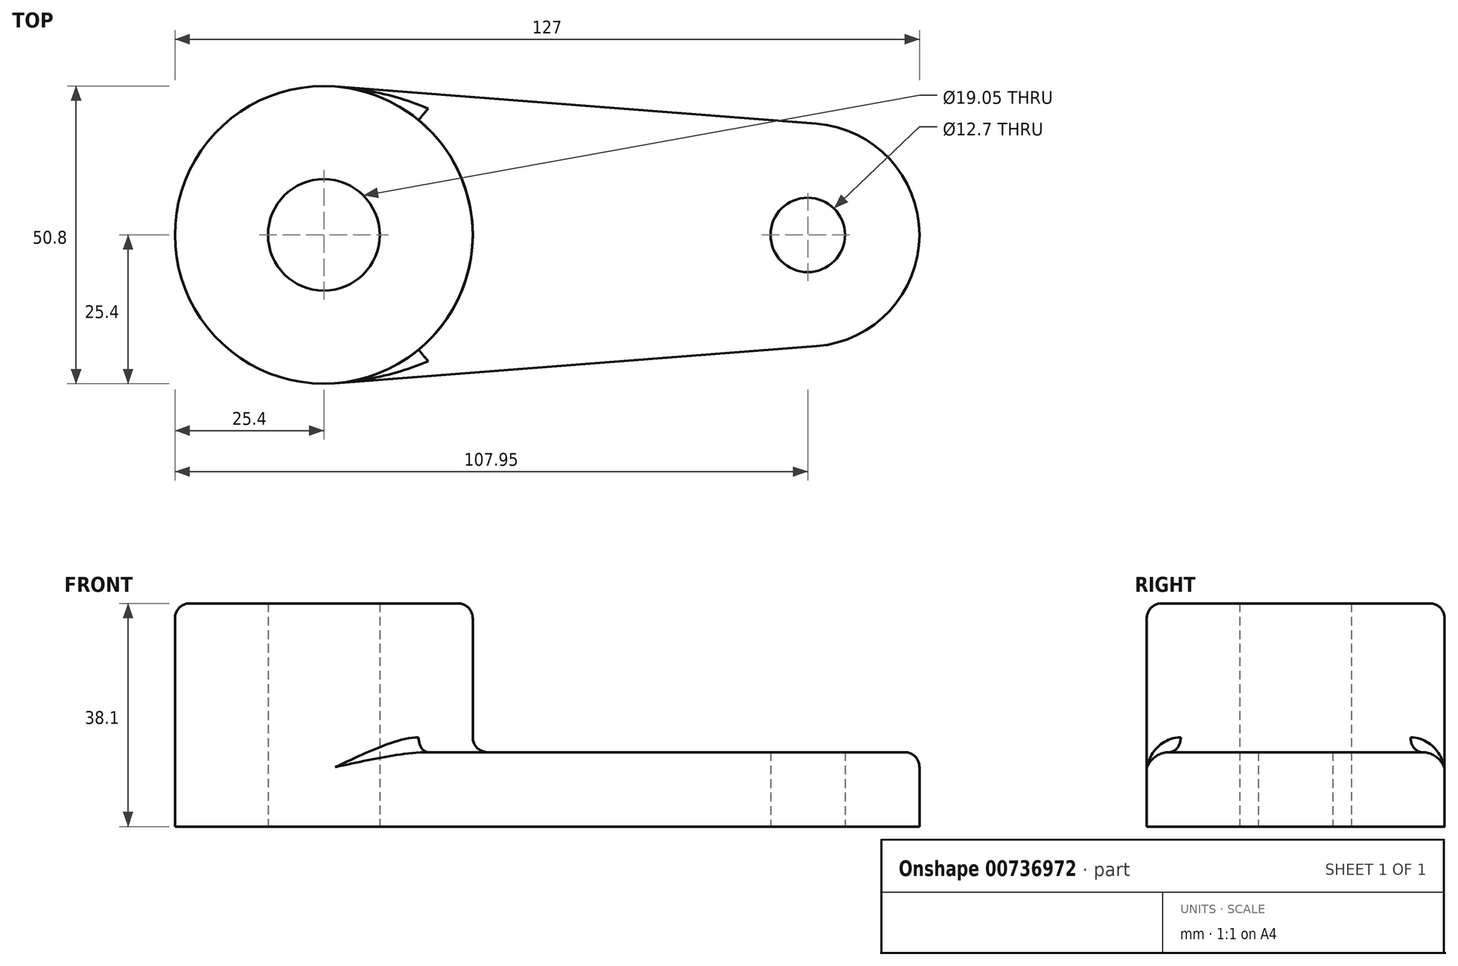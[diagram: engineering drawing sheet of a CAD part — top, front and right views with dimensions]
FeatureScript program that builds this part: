
annotation { "Feature Type Name" : "Feature", "Feature Type Description" : "" }
export const myFeature = defineFeature(function(context is Context, id is Id, definition is map)
    precondition{}
    {
        {
            var Q0;
            Q0=qCreatedBy(makeId("Top.planeOp"),FACE);
            var sketch = newSketch(context, id + "F0", { "sketchPlane" : qUnion([Q0])});
            skCircle(sketch, "E0", {"center": v(0, 0) * mm, "radius": 25.4 * mm});
            skCircle(sketch, "E1", {"center": v(82.55, 0) * mm, "radius": 19.05 * mm});
            skCircle(sketch, "E2", {"center": v(0, 0) * mm, "radius": 9.53 * mm});
            skCircle(sketch, "E3", {"center": v(82.55, 0) * mm, "radius": 6.35 * mm});
            skLineSegment(sketch, "E4", {"start": v(1.95, 25.32) * mm, "end": v(84.02, 19) * mm});
            skLineSegment(sketch, "E5", {"start": v(1.95, -25.32) * mm, "end": v(84.02, -19) * mm});
            skSolve(sketch);
        }
        {
            var Q0;
            Q0=makeQuery(id+"F0.imprint","IMPRINT",FACE,{"disambiguationData":[TD([[makeQuery(id+"F0.imprint","IMPRINT",EDGE,{"derivedFrom":sQuery(id+"F0.wireOp",EDGE,"E2")}),-1.0]])]});
            extrude(context, id + "F1", {"entities" : qUnion([Q0]), "depth" : 38.1 * mm, "offsetDistance" : 25.4 * mm});
        }
        {
            var Q0;
            Q0 = qSketchRegion(id + "F0", true);
            extrude(context, id + "F2", {"entities" : qUnion([Q0]), "operationType" : NewBodyOperationType.ADD, "depth" : 12.7 * mm, "offsetDistance" : 25.4 * mm});
        }
        {
            var Q0;
            Q0=makeQuery(id+"F1.opExtrude","CAP_EDGE",EDGE,{"disambiguationData":[OSD([sQuery(id+"F0.wireOp",EDGE,"E0")])],"isStart":false});
            var Q1;
            Q1=makeQuery(id+"F2.opExtrude","CAP_EDGE",EDGE,{"disambiguationData":[OSD([sQuery(id+"F0.wireOp",EDGE,"E5")])],"isStart":false});
            var Q2;
            {var subQ0=sQuery(id+"F0.wireOp",EDGE,"E0");Q2=makeQuery(id+"F2.boolean.opBoolean","INTERSECT",EDGE,{"derivedFrom":[makeQuery(id+"F1.opExtrude","SWEPT_FACE",FACE,{"disambiguationData":[OSD([subQ0])]}),makeQuery(id+"F2.opExtrude","CAP_FACE",FACE,{"disambiguationData":[OSD([subQ0,sQuery(id+"F0.wireOp",EDGE,"E1"),sQuery(id+"F0.wireOp",EDGE,"E2"),sQuery(id+"F0.wireOp",EDGE,"E3"),sQuery(id+"F0.wireOp",EDGE,"E4"),sQuery(id+"F0.wireOp",EDGE,"E5")])],"isStart":false})]});}
            fillet(context, id + "F3", {"entities" : qUnion([Q0, Q1, Q2]), "radius" : 2.54 * mm, "tangentPropagation" : true, "allowEdgeOverflow" : false});
        }
    });
